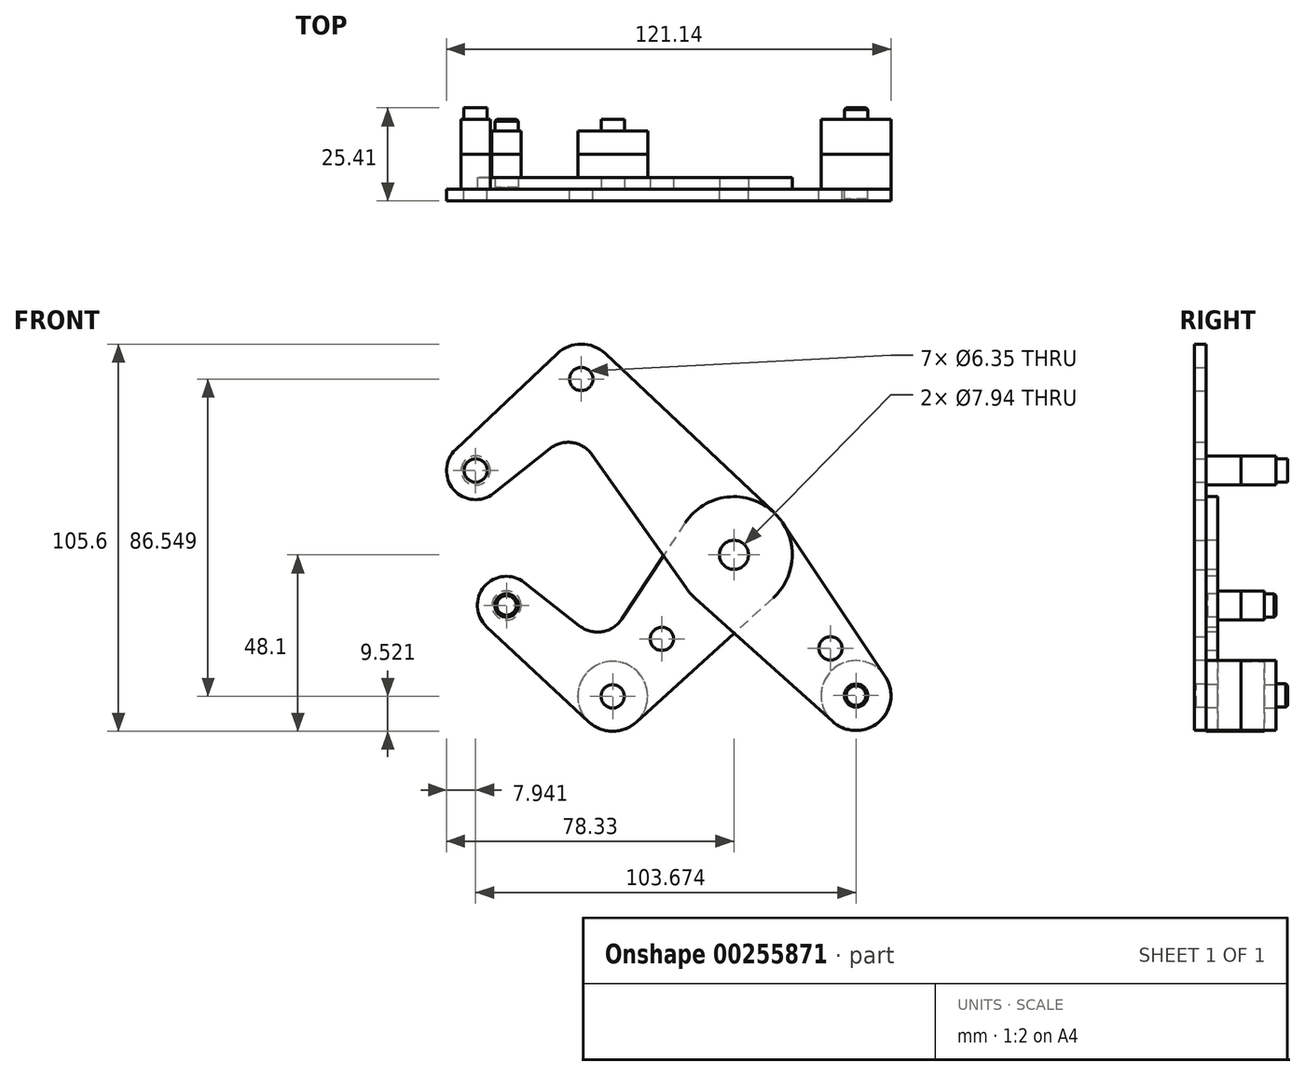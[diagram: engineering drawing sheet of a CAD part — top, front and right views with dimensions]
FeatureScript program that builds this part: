
annotation { "Feature Type Name" : "Feature", "Feature Type Description" : "" }
export const myFeature = defineFeature(function(context is Context, id is Id, definition is map)
    precondition{}
    {
        {
            var Q0;
            Q0=qCreatedBy(makeId("Front.planeOp"),FACE);
            var sketch = newSketch(context, id + "F0", { "sketchPlane" : qUnion([Q0])});
            skLineSegment(sketch, "E0", {"start": v(-41.6, 47.97) * mm, "end": v(41.6, -47.97) * mm, "construction": true});
            skCircle(sketch, "E1", {"center": v(0, 0) * mm, "radius": 3.18 * mm});
            skCircle(sketch, "E2", {"center": v(33.29, -38.38) * mm, "radius": 3.18 * mm});
            skCircle(sketch, "E3", {"center": v(-41.6, 47.97) * mm, "radius": 3.18 * mm});
            skCircle(sketch, "E4", {"center": v(-70.39, 23) * mm, "radius": 3.18 * mm});
            skLineSegment(sketch, "E5", {"start": v(-41.6, 47.97) * mm, "end": v(-70.39, 23) * mm, "construction": true});
            skCircle(sketch, "E6", {"center": v(33.29, -38.38) * mm, "radius": 9.53 * mm});
            skCircle(sketch, "E7", {"center": v(-70.39, 23) * mm, "radius": 7.94 * mm});
            skCircle(sketch, "E8", {"center": v(-41.6, 47.97) * mm, "radius": 9.53 * mm});
            skLineSegment(sketch, "E9", {"start": v(-75.83, 28.78) * mm, "end": v(-48.14, 54.9) * mm});
            skLineSegment(sketch, "E10", {"start": v(-65.44, 16.8) * mm, "end": v(-50.15, 28.98) * mm});
            skCircle(sketch, "E11", {"center": v(0, 0) * mm, "radius": 15.88 * mm});
            skLineSegment(sketch, "E12", {"start": v(-35.07, 54.9) * mm, "end": v(10.9, 11.55) * mm});
            skLineSegment(sketch, "E13", {"start": v(-38.72, 27.35) * mm, "end": v(-12.97, -9.15) * mm});
            skLineSegment(sketch, "E14", {"start": v(-10.6, -11.82) * mm, "end": v(26.93, -45.47) * mm});
            skLineSegment(sketch, "E15", {"start": v(13.2, 8.82) * mm, "end": v(41.2, -33.08) * mm});
            skArc(sketch, "E16.filletArc", {"start": v(-38.72, 27.35) * mm, "mid": v(-44.08, 30.63) * mm, "end": v(-50.15, 28.98) * mm});
            skLineSegment(sketch, "E17", {"start": v(0, 0) * mm, "end": v(-33.05, -38.58) * mm, "construction": true});
            skLineSegment(sketch, "E18", {"start": v(-33.05, -38.58) * mm, "end": v(-61.98, -13.8) * mm, "construction": true});
            skCircle(sketch, "E19", {"center": v(-61.98, -13.8) * mm, "radius": 3.18 * mm});
            skCircle(sketch, "E20", {"center": v(-33.05, -38.58) * mm, "radius": 3.18 * mm});
            skCircle(sketch, "E21", {"center": v(-61.98, -13.8) * mm, "radius": 7.94 * mm});
            skCircle(sketch, "E22", {"center": v(-33.05, -38.58) * mm, "radius": 9.53 * mm});
            skLineSegment(sketch, "E23", {"start": v(-57.08, -7.55) * mm, "end": v(-42.08, -19.35) * mm});
            skLineSegment(sketch, "E24", {"start": v(-67.4, -19.6) * mm, "end": v(-39.54, -45.55) * mm});
            skLineSegment(sketch, "E25", {"start": v(-13.25, 8.74) * mm, "end": v(-30.55, -17.48) * mm});
            skLineSegment(sketch, "E26", {"start": v(10.67, -11.75) * mm, "end": v(-26.65, -45.63) * mm});
            skArc(sketch, "E27.filletArc", {"start": v(-42.08, -19.35) * mm, "mid": v(-35.9, -20.95) * mm, "end": v(-30.55, -17.48) * mm});
            skCircle(sketch, "E28", {"center": v(-19.62, -22.9) * mm, "radius": 3.18 * mm});
            skCircle(sketch, "E29", {"center": v(26.32, -25.5) * mm, "radius": 3.18 * mm});
            skLineSegment(sketch, "E30", {"start": v(26.32, -25.5) * mm, "end": v(23.92, -27.58) * mm, "construction": true});
            skCircle(sketch, "E31", {"center": v(0, 0) * mm, "radius": 3.97 * mm});
            skSolve(sketch);
        }
        {
            var Q0;
            Q0=qCreatedBy(makeId("Front.planeOp"),FACE);
            cPlane(context, id + "F1", {"entities" : qUnion([Q0]), "cplaneType" : CPlaneType.OFFSET, "offset" : 9.52 * mm, "oppositeDirection" : true, "width" : 254 * mm, "height" : 254 * mm});
        }
        {
            var Q0;
            Q0=makeQuery(id+"F0.imprint","IMPRINT",FACE,{"disambiguationData":[TD([[makeQuery(id+"F0.imprint","IMPRINT",EDGE,{"derivedFrom":sQuery(id+"F0.wireOp",EDGE,"E4")}),-1.0]])]});
            var Q1;
            Q1=makeQuery(id+"F0.imprint","IMPRINT",FACE,{"disambiguationData":[TD([[makeQuery(id+"F0.imprint","IMPRINT",EDGE,{"derivedFrom":sQuery(id+"F0.wireOp",EDGE,"E3")}),-1.0]])]});
            var Q2;
            {var subQ1=sQuery(id+"F0.wireOp",EDGE,"E9");Q2=makeQuery(id+"F0.imprint","IMPRINT",FACE,{"disambiguationData":[TD([[makeQuery(id+"F0.imprint","IMPRINT",EDGE,{"derivedFrom":subQ1}),-1.0]])]});}
            var Q3;
            Q3=makeQuery(id+"F0.imprint","IMPRINT",FACE,{"disambiguationData":[TD([[makeQuery(id+"F0.imprint","IMPRINT",EDGE,{"derivedFrom":sQuery(id+"F0.wireOp",EDGE,"E31")}),-1.0]])]});
            var Q4;
            {var subQ0=sQuery(id+"F0.wireOp",EDGE,"E13");var subQ1=sQuery(id+"F0.wireOp",EDGE,"E11");var subQ2=makeQuery(id+"F0.imprint","INTERSECT",VERTEX,{"derivedFrom":[subQ1,subQ0]});Q4=makeQuery(id+"F0.imprint","IMPRINT",FACE,{"disambiguationData":[TD([[makeQuery(id+"F0.imprint","IMPRINT",EDGE,{"disambiguationData":[TD([[subQ2,1.0]])],"derivedFrom":subQ1}),-1.0]])]});}
            var Q5;
            {var subQ0=sQuery(id+"F0.wireOp",EDGE,"E14");var subQ1=sQuery(id+"F0.wireOp",EDGE,"E11");var subQ2=makeQuery(id+"F0.imprint","INTERSECT",VERTEX,{"derivedFrom":[subQ1,subQ0]});Q5=makeQuery(id+"F0.imprint","IMPRINT",FACE,{"disambiguationData":[TD([[makeQuery(id+"F0.imprint","IMPRINT",EDGE,{"disambiguationData":[TD([[subQ2,-1.0]])],"derivedFrom":subQ1}),-1.0]])]});}
            var Q6;
            {var subQ0=sQuery(id+"F0.wireOp",EDGE,"E15");Q6=makeQuery(id+"F0.imprint","IMPRINT",FACE,{"disambiguationData":[TD([[makeQuery(id+"F0.imprint","IMPRINT",EDGE,{"derivedFrom":subQ0}),-1.0]])]});}
            var Q7;
            Q7=makeQuery(id+"F0.imprint","IMPRINT",FACE,{"disambiguationData":[TD([[makeQuery(id+"F0.imprint","IMPRINT",EDGE,{"derivedFrom":sQuery(id+"F0.wireOp",EDGE,"E2")}),-1.0]])]});
            extrude(context, id + "F2", {"entities" : qUnion([Q0, Q1, Q2, Q3, Q4, Q5, Q6, Q7]), "depth" : 3.17 * mm});
        }
        {
            var Q0;
            Q0=makeQuery(id+"F0.imprint","IMPRINT",FACE,{"disambiguationData":[TD([[makeQuery(id+"F0.imprint","IMPRINT",EDGE,{"derivedFrom":sQuery(id+"F0.wireOp",EDGE,"E31")}),-1.0]])]});
            var Q1;
            {var subQ0=sQuery(id+"F0.wireOp",EDGE,"E14");var subQ1=sQuery(id+"F0.wireOp",EDGE,"E11");var subQ2=makeQuery(id+"F0.imprint","INTERSECT",VERTEX,{"derivedFrom":[subQ1,subQ0]});Q1=makeQuery(id+"F0.imprint","IMPRINT",FACE,{"disambiguationData":[TD([[makeQuery(id+"F0.imprint","IMPRINT",EDGE,{"disambiguationData":[TD([[subQ2,-1.0]])],"derivedFrom":subQ1}),-1.0]])]});}
            var Q2;
            {var subQ10=sQuery(id+"F0.wireOp",EDGE,"E23");Q2=makeQuery(id+"F0.imprint","IMPRINT",FACE,{"disambiguationData":[TD([[makeQuery(id+"F0.imprint","IMPRINT",EDGE,{"derivedFrom":subQ10}),-1.0]])]});}
            var Q3;
            Q3=makeQuery(id+"F0.imprint","IMPRINT",FACE,{"disambiguationData":[TD([[makeQuery(id+"F0.imprint","IMPRINT",EDGE,{"derivedFrom":sQuery(id+"F0.wireOp",EDGE,"E20")}),-1.0]])]});
            var Q4;
            Q4=makeQuery(id+"F0.imprint","IMPRINT",FACE,{"disambiguationData":[TD([[makeQuery(id+"F0.imprint","IMPRINT",EDGE,{"derivedFrom":sQuery(id+"F0.wireOp",EDGE,"E19")}),-1.0]])]});
            var Q5;
            {var subQ0=sQuery(id+"F0.wireOp",EDGE,"E13");var subQ1=sQuery(id+"F0.wireOp",EDGE,"E11");var subQ2=makeQuery(id+"F0.imprint","INTERSECT",VERTEX,{"derivedFrom":[subQ1,subQ0]});Q5=makeQuery(id+"F0.imprint","IMPRINT",FACE,{"disambiguationData":[TD([[makeQuery(id+"F0.imprint","IMPRINT",EDGE,{"disambiguationData":[TD([[subQ2,1.0]])],"derivedFrom":subQ1}),-1.0]])]});}
            extrude(context, id + "F3", {"entities" : qUnion([Q0, Q1, Q2, Q3, Q4, Q5]), "oppositeDirection" : true, "depth" : 3.17 * mm});
        }
        {
            var Q0;
            Q0=makeQuery(id+"F2.opExtrude","CAP_FACE",FACE,{"disambiguationData":[OSD([sQuery(id+"F0.wireOp",EDGE,"E2"),sQuery(id+"F0.wireOp",EDGE,"E3"),sQuery(id+"F0.wireOp",EDGE,"E4"),sQuery(id+"F0.wireOp",EDGE,"E6"),sQuery(id+"F0.wireOp",EDGE,"E7"),sQuery(id+"F0.wireOp",EDGE,"E8"),sQuery(id+"F0.wireOp",EDGE,"E9"),sQuery(id+"F0.wireOp",EDGE,"E10"),sQuery(id+"F0.wireOp",EDGE,"E11"),sQuery(id+"F0.wireOp",EDGE,"E12"),sQuery(id+"F0.wireOp",EDGE,"E13"),sQuery(id+"F0.wireOp",EDGE,"E14"),sQuery(id+"F0.wireOp",EDGE,"E15"),sQuery(id+"F0.wireOp",EDGE,"E16.filletArc"),sQuery(id+"F0.wireOp",EDGE,"E29"),sQuery(id+"F0.wireOp",EDGE,"E31")])],"isStart":false});
            var sketch = newSketch(context, id + "F4", { "sketchPlane" : qUnion([Q0])});
            skCircle(sketch, "E32", {"center": v(33.29, -38.38) * mm, "radius": 9.53 * mm});
            skCircle(sketch, "E33", {"center": v(-70.39, 23) * mm, "radius": 3.98 * mm});
            skSolve(sketch);
        }
        {
            var Q0;
            Q0=makeQuery(id+"F3.opExtrude","CAP_FACE",FACE,{"disambiguationData":[OSD([sQuery(id+"F0.wireOp",EDGE,"E11"),sQuery(id+"F0.wireOp",EDGE,"E19"),sQuery(id+"F0.wireOp",EDGE,"E20"),sQuery(id+"F0.wireOp",EDGE,"E21"),sQuery(id+"F0.wireOp",EDGE,"E22"),sQuery(id+"F0.wireOp",EDGE,"E23"),sQuery(id+"F0.wireOp",EDGE,"E24"),sQuery(id+"F0.wireOp",EDGE,"E25"),sQuery(id+"F0.wireOp",EDGE,"E26"),sQuery(id+"F0.wireOp",EDGE,"E27.filletArc"),sQuery(id+"F0.wireOp",EDGE,"E28"),sQuery(id+"F0.wireOp",EDGE,"E31")])],"isStart":true});
            var sketch = newSketch(context, id + "F5", { "sketchPlane" : qUnion([Q0])});
            skCircle(sketch, "E34", {"center": v(-33.05, -38.58) * mm, "radius": 9.53 * mm});
            skCircle(sketch, "E35", {"center": v(-61.98, -13.8) * mm, "radius": 3.98 * mm});
            skSolve(sketch);
        }
        {
            var Q0;
            Q0 = qSketchRegion(id + "F4", true);
            var Q1;
            Q1 = qSketchRegion(id + "F5", true);
            var Q2;
            Q2=qCreatedBy(id+"F1.planeOp",FACE);
            extrude(context, id + "F6", {"entities" : qUnion([Q0, Q1]), "endBound" : BoundingType.UP_TO_SURFACE, "oppositeDirection" : true, "endBoundEntityFace" : qUnion([Q2]), "depth" : 25.4 * mm});
        }
        {
            var Q0;
            Q0=makeQuery(id+"F2.opExtrude","SWEPT_BODY",BODY,{"disambiguationData":[OSD([sQuery(id+"F0.wireOp",EDGE,"E2"),sQuery(id+"F0.wireOp",EDGE,"E3"),sQuery(id+"F0.wireOp",EDGE,"E4"),sQuery(id+"F0.wireOp",EDGE,"E6"),sQuery(id+"F0.wireOp",EDGE,"E7"),sQuery(id+"F0.wireOp",EDGE,"E8"),sQuery(id+"F0.wireOp",EDGE,"E9"),sQuery(id+"F0.wireOp",EDGE,"E10"),sQuery(id+"F0.wireOp",EDGE,"E11"),sQuery(id+"F0.wireOp",EDGE,"E12"),sQuery(id+"F0.wireOp",EDGE,"E13"),sQuery(id+"F0.wireOp",EDGE,"E14"),sQuery(id+"F0.wireOp",EDGE,"E15"),sQuery(id+"F0.wireOp",EDGE,"E16.filletArc"),sQuery(id+"F0.wireOp",EDGE,"E29"),sQuery(id+"F0.wireOp",EDGE,"E31")])]});
            var Q1;
            Q1=makeQuery(id+"F3.opExtrude","SWEPT_BODY",BODY,{"disambiguationData":[OSD([sQuery(id+"F0.wireOp",EDGE,"E11"),sQuery(id+"F0.wireOp",EDGE,"E19"),sQuery(id+"F0.wireOp",EDGE,"E20"),sQuery(id+"F0.wireOp",EDGE,"E21"),sQuery(id+"F0.wireOp",EDGE,"E22"),sQuery(id+"F0.wireOp",EDGE,"E23"),sQuery(id+"F0.wireOp",EDGE,"E24"),sQuery(id+"F0.wireOp",EDGE,"E25"),sQuery(id+"F0.wireOp",EDGE,"E26"),sQuery(id+"F0.wireOp",EDGE,"E27.filletArc"),sQuery(id+"F0.wireOp",EDGE,"E28"),sQuery(id+"F0.wireOp",EDGE,"E31")])]});
            var Q2;
            Q2=makeQuery(id+"F6.opExtrude","SWEPT_BODY",BODY,{"disambiguationData":[OSD([sQuery(id+"F4.wireOp",EDGE,"E33")])]});
            var Q3;
            Q3=makeQuery(id+"F6.opExtrude","SWEPT_BODY",BODY,{"disambiguationData":[OSD([sQuery(id+"F5.wireOp",EDGE,"E35")])]});
            var Q4;
            Q4=makeQuery(id+"F6.opExtrude","SWEPT_BODY",BODY,{"disambiguationData":[OSD([sQuery(id+"F5.wireOp",EDGE,"E34")])]});
            var Q5;
            Q5=makeQuery(id+"F6.opExtrude","SWEPT_BODY",BODY,{"disambiguationData":[OSD([sQuery(id+"F4.wireOp",EDGE,"E32")])]});
            booleanBodies(context, id + "F7", {"operationType" : BooleanOperationType.SUBTRACTION, "tools" : qUnion([Q0, Q1]), "targets" : qUnion([Q2, Q3, Q4, Q5]), "keepTools" : true});
        }
        {
            var Q0;
            Q0=makeQuery(id+"F7.opBoolean","COPY",EDGE,{"derivedFrom":makeQuery(id+"F2.opExtrude","CAP_EDGE",EDGE,{"disambiguationData":[OSD([sQuery(id+"F0.wireOp",EDGE,"E4")])],"isStart":false})});
            var Q1;
            Q1=makeQuery(id+"F6.opExtrude","CAP_FACE",FACE,{"disambiguationData":[OSD([sQuery(id+"F5.wireOp",EDGE,"E35")])],"isStart":true});
            var Q2;
            Q2=makeQuery(id+"F7.opBoolean","COPY",EDGE,{"derivedFrom":makeQuery(id+"F3.opExtrude","CAP_EDGE",EDGE,{"disambiguationData":[OSD([sQuery(id+"F0.wireOp",EDGE,"E20")])],"isStart":true})});
            var Q3;
            Q3=makeQuery(id+"F6.opExtrude","CAP_FACE",FACE,{"disambiguationData":[OSD([sQuery(id+"F4.wireOp",EDGE,"E32")])],"isStart":true});
            chamfer(context, id + "F8", {"entities" : qUnion([Q0, Q1, Q2, Q3]), "width" : 0.5 * mm, "tangentPropagation" : true});
        }
        {
            var Q0;
            Q0=makeQuery(id+"F6.opExtrude","SWEPT_BODY",BODY,{"disambiguationData":[OSD([sQuery(id+"F5.wireOp",EDGE,"E35")])]});
            var Q1;
            Q1=makeQuery(id+"F6.opExtrude","SWEPT_BODY",BODY,{"disambiguationData":[OSD([sQuery(id+"F5.wireOp",EDGE,"E34")])]});
            var Q2;
            Q2=makeQuery(id+"F6.opExtrude","SWEPT_BODY",BODY,{"disambiguationData":[OSD([sQuery(id+"F4.wireOp",EDGE,"E33")])]});
            var Q3;
            Q3=makeQuery(id+"F6.opExtrude","SWEPT_BODY",BODY,{"disambiguationData":[OSD([sQuery(id+"F4.wireOp",EDGE,"E32")])]});
            var Q4;
            Q4=qCreatedBy(id+"F1.planeOp",FACE);
            mirror(context, id + "F9", {"entities" : qUnion([Q0, Q1, Q2, Q3]), "mirrorPlane" : qUnion([Q4])});
        }
    });
